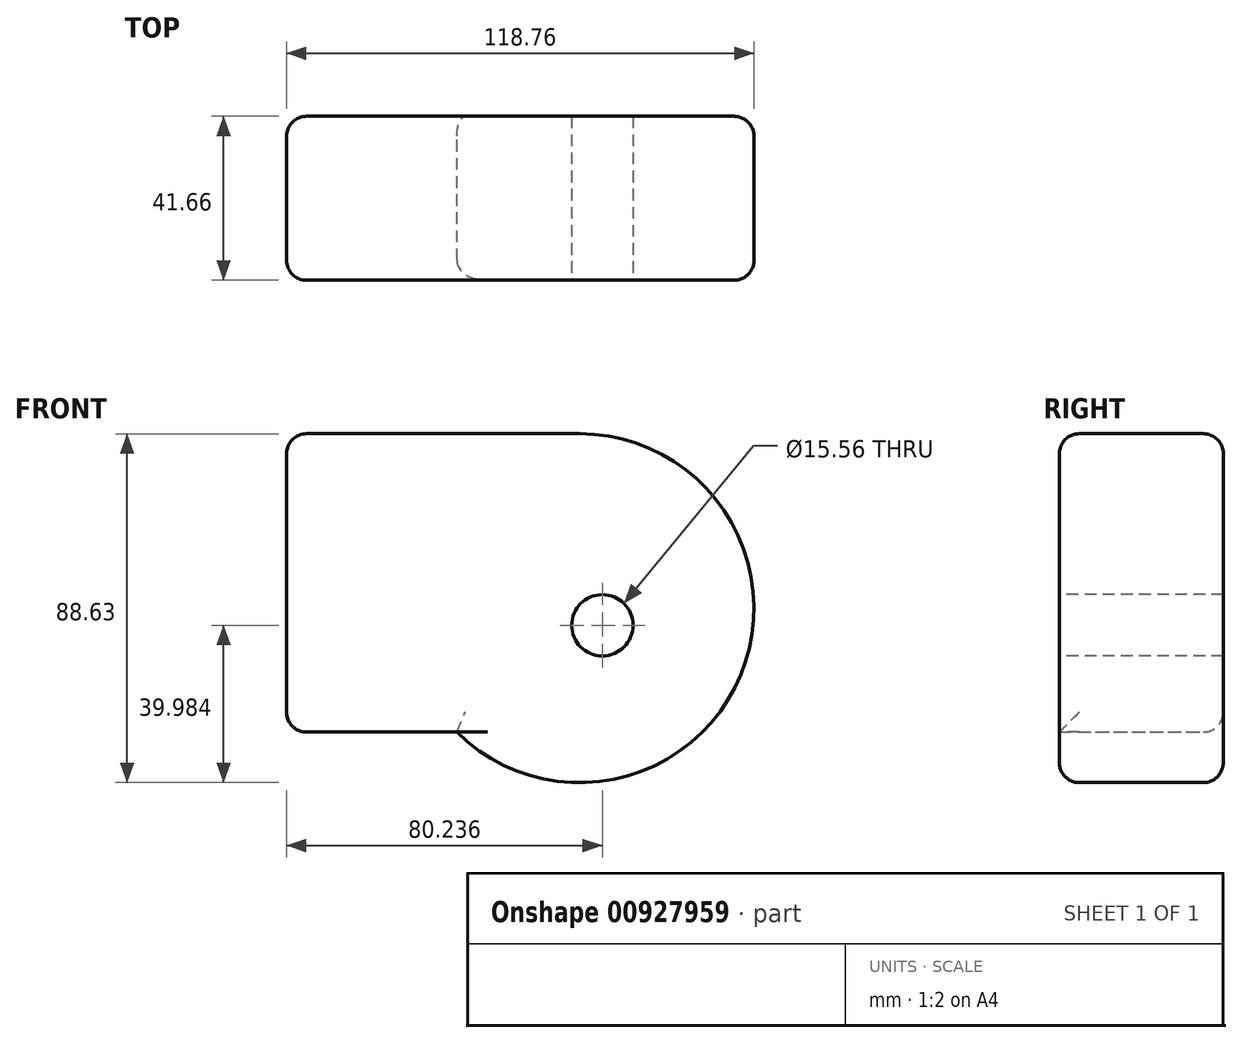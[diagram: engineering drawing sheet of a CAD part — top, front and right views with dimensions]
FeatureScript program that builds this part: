
annotation { "Feature Type Name" : "Feature", "Feature Type Description" : "" }
export const myFeature = defineFeature(function(context is Context, id is Id, definition is map)
    precondition{}
    {
        {
            var Q0;
            Q0=qCreatedBy(makeId("Front.planeOp"),FACE);
            var sketch = newSketch(context, id + "F0", { "sketchPlane" : qUnion([Q0])});
            skLineSegment(sketch, "E0.bottom", {"start": v(-37.22, 37.9) * mm, "end": v(37.22, 37.9) * mm});
            skLineSegment(sketch, "E0.top", {"start": v(-37.22, -37.9) * mm, "end": v(37.22, -37.9) * mm});
            skLineSegment(sketch, "E0.left", {"start": v(-37.22, 37.9) * mm, "end": v(-37.22, -37.9) * mm});
            skLineSegment(sketch, "E0.right", {"start": v(37.22, 37.9) * mm, "end": v(37.22, -37.9) * mm});
            skPoint(sketch, "E0.middle", {"position": v(0, 0) * mm});
            skCircle(sketch, "E1", {"center": v(37.22, -6.41) * mm, "radius": 44.32 * mm});
            skSolve(sketch);
        }
        {
            var Q0;
            {var subQ0=sQuery(id+"F0.wireOp",EDGE,"E0.right");Q0=makeQuery(id+"F0.imprint","IMPRINT",FACE,{"disambiguationData":[TD([[makeQuery(id+"F0.imprint","IMPRINT",EDGE,{"derivedFrom":subQ0}),-1.0]])]});}
            var Q1;
            {var subQ0=sQuery(id+"F0.wireOp",EDGE,"E0.right");Q1=makeQuery(id+"F0.imprint","IMPRINT",FACE,{"disambiguationData":[TD([[makeQuery(id+"F0.imprint","IMPRINT",EDGE,{"derivedFrom":subQ0}),1.0]])]});}
            var Q2;
            {var subQ0=sQuery(id+"F0.wireOp",EDGE,"E0.bottom");Q2=makeQuery(id+"F0.imprint","IMPRINT",FACE,{"disambiguationData":[TD([[makeQuery(id+"F0.imprint","IMPRINT",EDGE,{"derivedFrom":subQ0}),-1.0]])]});}
            extrude(context, id + "F1", {"entities" : qUnion([Q0, Q1, Q2]), "depth" : 41.66 * mm, "offsetDistance" : 25.4 * mm});
        }
        {
            var Q0;
            Q0=makeQuery(id+"F1.opExtrude","CAP_EDGE",EDGE,{"disambiguationData":[OSD([sQuery(id+"F0.wireOp",EDGE,"E0.bottom")])],"isStart":false});
            var Q1;
            Q1=makeQuery(id+"F1.opExtrude","SWEPT_EDGE",EDGE,{"disambiguationData":[OSD([sQuery(id+"F0.wireOp",EDGE,"E0.bottom"),sQuery(id+"F0.wireOp",EDGE,"E0.right"),sQuery(id+"F0.wireOp",EDGE,"E1")])]});
            var Q2;
            Q2=makeQuery(id+"F1.opExtrude","CAP_EDGE",EDGE,{"disambiguationData":[OSD([sQuery(id+"F0.wireOp",EDGE,"E1")])],"isStart":true});
            var Q3;
            Q3=makeQuery(id+"F1.opExtrude","CAP_EDGE",EDGE,{"disambiguationData":[OSD([sQuery(id+"F0.wireOp",EDGE,"E0.top")])],"isStart":true});
            var Q4;
            Q4=makeQuery(id+"F1.opExtrude","CAP_EDGE",EDGE,{"disambiguationData":[OSD([sQuery(id+"F0.wireOp",EDGE,"E0.left")])],"isStart":true});
            var Q5;
            Q5=makeQuery(id+"F1.opExtrude","SWEPT_EDGE",EDGE,{"disambiguationData":[OSD([sQuery(id+"F0.wireOp",EDGE,"E0.bottom"),sQuery(id+"F0.wireOp",EDGE,"E0.left")])]});
            var Q6;
            Q6=makeQuery(id+"F1.opExtrude","CAP_EDGE",EDGE,{"disambiguationData":[OSD([sQuery(id+"F0.wireOp",EDGE,"E0.left")])],"isStart":false});
            var Q7;
            Q7=makeQuery(id+"F1.opExtrude","SWEPT_EDGE",EDGE,{"disambiguationData":[OSD([sQuery(id+"F0.wireOp",EDGE,"E0.top"),sQuery(id+"F0.wireOp",EDGE,"E0.left")])]});
            fillet(context, id + "F2", {"entities" : qUnion([Q0, Q1, Q2, Q3, Q4, Q5, Q6, Q7]), "radius" : 5.08 * mm, "tangentPropagation" : true, "allowEdgeOverflow" : false});
        }
        {
            var Q0;
            Q0=makeQuery(id+"F1.opExtrude","CAP_FACE",FACE,{"disambiguationData":[OSD([sQuery(id+"F0.wireOp",EDGE,"E0.bottom"),sQuery(id+"F0.wireOp",EDGE,"E0.top"),sQuery(id+"F0.wireOp",EDGE,"E0.left"),sQuery(id+"F0.wireOp",EDGE,"E1")])],"isStart":false});
            var sketch = newSketch(context, id + "F3", { "sketchPlane" : qUnion([Q0])});
            skCircle(sketch, "E2", {"center": v(43.02, -10.75) * mm, "radius": 7.78 * mm});
            skSolve(sketch);
        }
        {
            var Q0;
            Q0=makeQuery(id+"F3.imprint","IMPRINT",FACE,{"disambiguationData":[TD([[makeQuery(id+"F3.imprint","IMPRINT",EDGE,{"derivedFrom":sQuery(id+"F3.wireOp",EDGE,"E2")}),1.0]])]});
            extrude(context, id + "F4", {"entities" : qUnion([Q0]), "operationType" : NewBodyOperationType.REMOVE, "oppositeDirection" : true, "depth" : 55.63 * mm, "offsetDistance" : 25.4 * mm});
        }
    });
